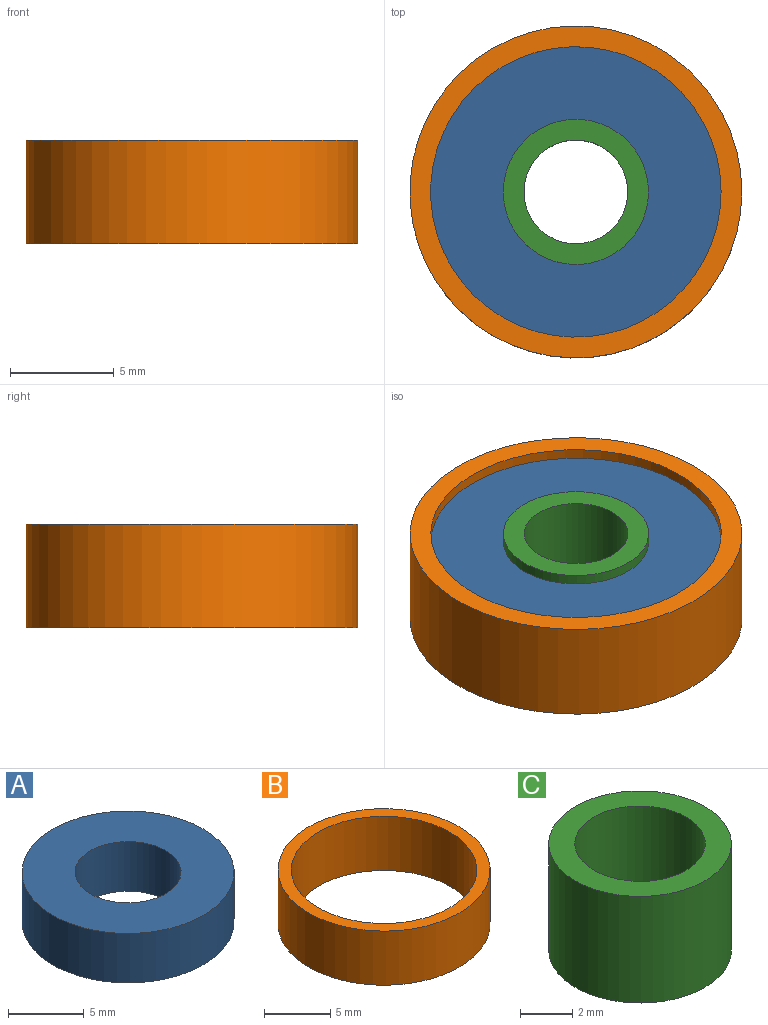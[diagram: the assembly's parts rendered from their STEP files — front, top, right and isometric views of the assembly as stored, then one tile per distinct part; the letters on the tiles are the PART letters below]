
ASSEMBLY  parts=3 mates=2
PART A: 4 faces, bbox 14x14x4 mm
  f0: cylinder r=3.5mm len=7mm, axis (0,0,-1), area 88mm2, adj f2,f3
  f1: cylinder r=7mm len=14mm, axis (0,0,-1), area 175.9mm2, adj f2,f3
  f2: plane 14x14mm, normal (0,0,1), area 115.5mm2, adj f0,f1
  f3: plane 14x14mm, normal (0,0,-1), area 115.5mm2, adj f0,f1
PART B: 4 faces, bbox 16x16x5 mm
  f0: cylinder r=7mm len=14mm, axis (0,0,-1), area 219.9mm2, adj f2,f3
  f1: cylinder r=8mm len=16mm, axis (0,0,-1), area 251.3mm2, adj f2,f3
  f2: plane 16x16mm, normal (0,0,1), area 47.1mm2, adj f0,f1
  f3: plane 16x16mm, normal (0,0,-1), area 47.1mm2, adj f0,f1
PART C: 4 faces, bbox 7x7x5 mm
  f0: cylinder r=2.5mm len=5mm, axis (0,0,-1), area 78.5mm2, adj f2,f3
  f1: cylinder r=3.5mm len=7mm, axis (0,0,-1), area 110mm2, adj f2,f3
  f2: plane 7x7mm, normal (0,0,1), area 18.8mm2, adj f0,f1
  f3: plane 7x7mm, normal (0,0,-1), area 18.8mm2, adj f0,f1
PLACE A t=(-7.29,-3,-0.18)mm
PLACE B t=(-7.29,-3,-0.68)mm
PLACE C t=(-7.29,-3,-0.68)mm
MATE revolute C.f1 <-> A.f0  axis (0,0,-1) through (-7.29,-3,1.82)mm
MATE revolute A.f1 <-> B.f0  axis (0,0,-1) through (-7.29,-3,1.82)mm
